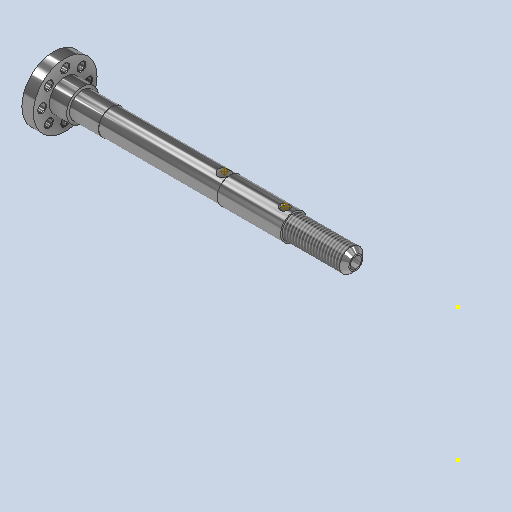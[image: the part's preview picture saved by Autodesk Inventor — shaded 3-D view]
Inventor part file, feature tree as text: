
AUTODESK INVENTOR PART (.ipt)
format: ipt  version: 2022 (Build 260153000, 153)  size: 269,312 bytes
history: native  units: in
note: dims shown in document units (in); Inventor stores cm internally (conversion verified against a paired STEP export)
features: sketch x10, plane x5, extrude x4, other x4, revolve x3, chamfer x3, thread x2
ambient origin geometry x8: Origin, YZ Plane, XZ Plane, XY Plane, X Axis, Y Axis, Z Axis, Center Point
bodies: Solid1 (feature_tree)
feature tree (31):
  revolve  "Revolution1"  [1 undecoded]
  plane  "Work Plane2"
  extrude  "Extrusion1"  Depth=0.8465in
  sketch  "Sketch4"  dims[d12=0.4331in d13=0.3465in]
  extrude  "Extrusion2"  Depth=0.3465in
  sketch  "Sketch6"  dims[d16=0.3543in d17=0.3543in]
  plane  "Work Plane3"
  revolve  "Revolution2"  [1 undecoded]
  revolve  "Revolution3"  [1 undecoded]
  extrude  "Extrusion8"  TaperAngle=90.0deg  [1 undecoded]
  chamfer  "Chamfer1"  Distance=0.1732in
  chamfer  "Chamfer2"  Distance=1.7913in
  plane  "Work Plane5"
  extrude  "Extrusion9"  TaperAngle=90.0deg  [1 undecoded]
  chamfer  "Chamfer3"  Distance=0.8661in
  sketch  "Sketch18"  dims[d39=0.6299in d40=0.8661in d41=120.0deg d42=0.2874in d43=0.315in d44=0.1063in d45=3.1496in d47=360.0deg d49=0.3937in d50=0.0in d51=0.0079in d52=0.0787in d53=45.0deg d54=0.063in d55=0.0787in d56=45.0deg d57=-0.9646in d58=0.0984in d59=0.3937in d60=0.0in d61=0.0197in d62=0.0787in d63=45.0deg d66=0.7835in d67=0.0in d68=0.1098in d69=0.0in]
  thread  "Thread1"  [1 undecoded]
  thread  "Thread2"  [1 undecoded]
  sketch  "Sketch2"  dims[d8=4.1142in d9=3.9567in]
  plane  "Work Plane1"
  other  "Work Axis1"
  other  "Work Point1"
  sketch  "Sketch3"  dims[d10=3.7205in d11=0.8465in]
  sketch  "Sketch5"  dims[d14=3.3268in d15=1.7126in]
  sketch  "Sketch10"  dims[d18=0.315in d19=90.0deg]
  sketch  "Sketch14"  dims[d20=-1.7913in d21=0.1732in d22=0.0in d23=1.7913in d24=0.0in]
  sketch  "Sketch15"  dims[d26=90.0deg d37=90.0deg]
  plane  "Work Plane4"
  other  "Work Axis2"
  other  "Work Point2"
  sketch  "Sketch16"  dims[d38=90.0deg]
note: 7 required parameter values undecoded (feature->parameter linkage not recoverable at this tier; creation-order binding heuristic only, values carry confidence <= 0.55)